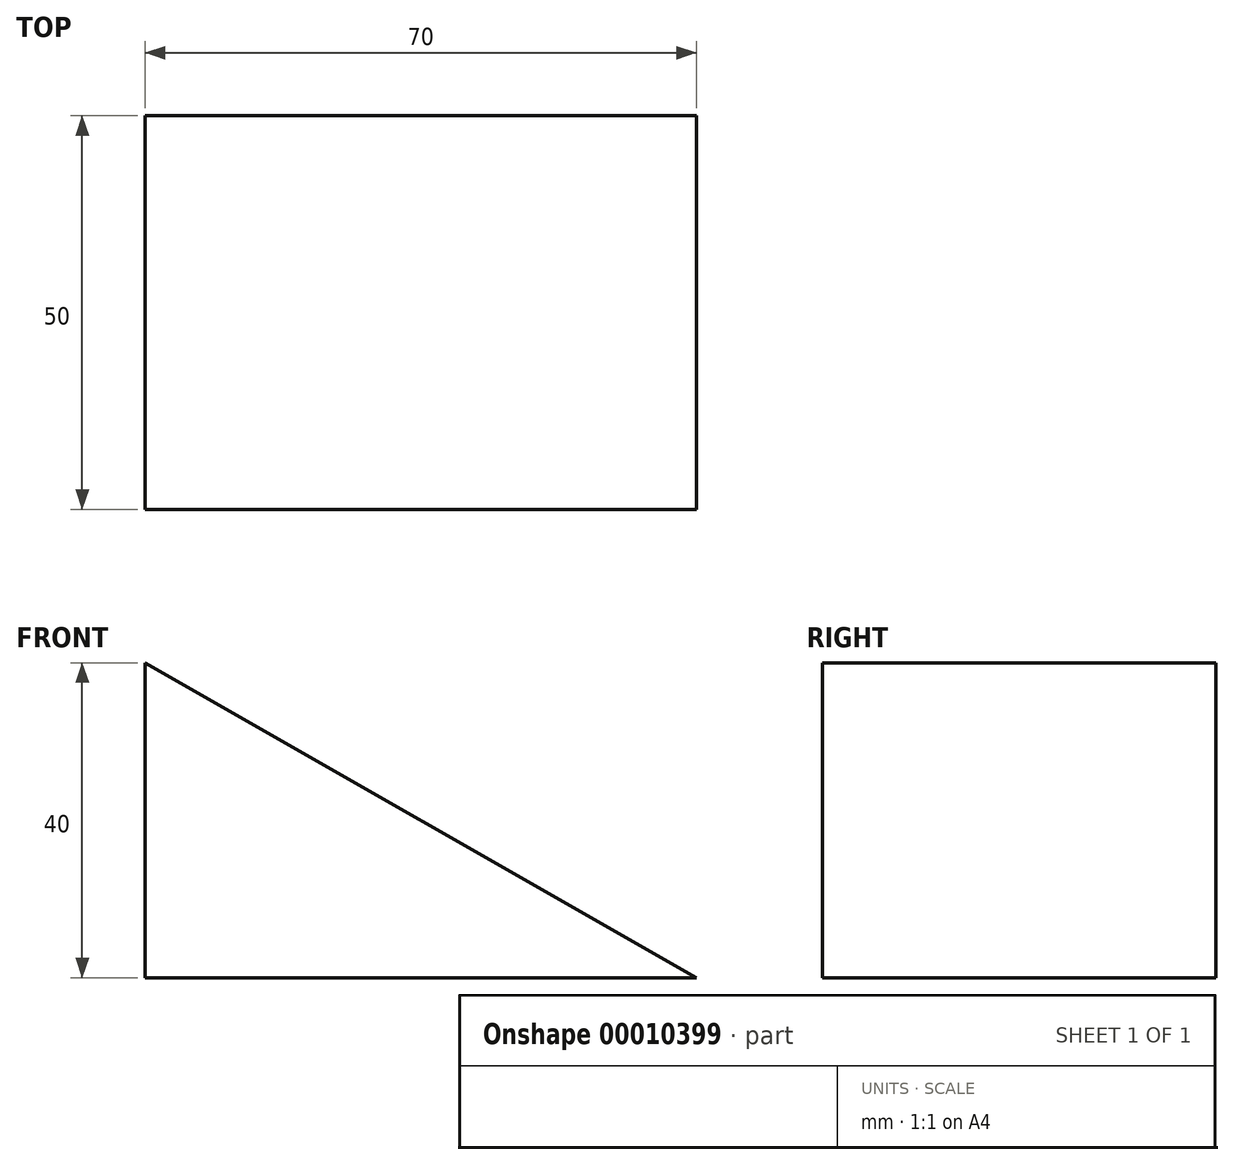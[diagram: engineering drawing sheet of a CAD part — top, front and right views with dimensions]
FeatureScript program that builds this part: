
annotation { "Feature Type Name" : "Feature", "Feature Type Description" : "" }
export const myFeature = defineFeature(function(context is Context, id is Id, definition is map)
    precondition{}
    {
        {
            var Q0;
            Q0=qCreatedBy(makeId("Front.planeOp"),FACE);
            var sketch = newSketch(context, id + "F0", { "sketchPlane" : qUnion([Q0])});
            skLineSegment(sketch, "E0", {"start": v(0, 0) * mm, "end": v(70, 0) * mm});
            skLineSegment(sketch, "E1", {"start": v(70, 0) * mm, "end": v(0, 40) * mm});
            skLineSegment(sketch, "E2", {"start": v(0, 40) * mm, "end": v(0, 0) * mm});
            skSolve(sketch);
        }
        {
            var Q0;
            Q0 = qSketchRegion(id + "F0", true);
            extrude(context, id + "F1", {"entities" : qUnion([Q0]), "oppositeDirection" : true, "depth" : 50 * mm});
        }
    });
